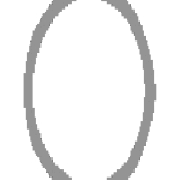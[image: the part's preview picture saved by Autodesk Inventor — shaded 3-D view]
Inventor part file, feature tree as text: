
AUTODESK INVENTOR PART (.ipt)
format: ipt  version: 2021 (Build 250183000, 183)  size: 112,640 bytes
history: native  units: in
note: dims shown in document units (in); Inventor stores cm internally (conversion verified against a paired STEP export)
features: other x4, sketch x3, plane x1
ambient origin geometry x8: Origin, YZ Plane, XZ Plane, XY Plane, X Axis, Y Axis, Z Axis, Center Point
bodies: Solid1 (feature_tree), Body (feature_tree)
feature tree (8):
  other  "Driven Length"
  other  "Frame Generator"
  other  "Start Plane"
  other  "End Plane"
  sketch  "Sketch"  dims[d2=16.9706in d4=-0.0in d5=16.9706in d6=0.12in d7=0.0in d8=90.0deg d9=16.9706in]
  sketch  "Sketch2"  dims[d0=1.0in]
  plane  "Work Plane3"
  sketch  "Sketch3"  dims[d1=0.065in]
